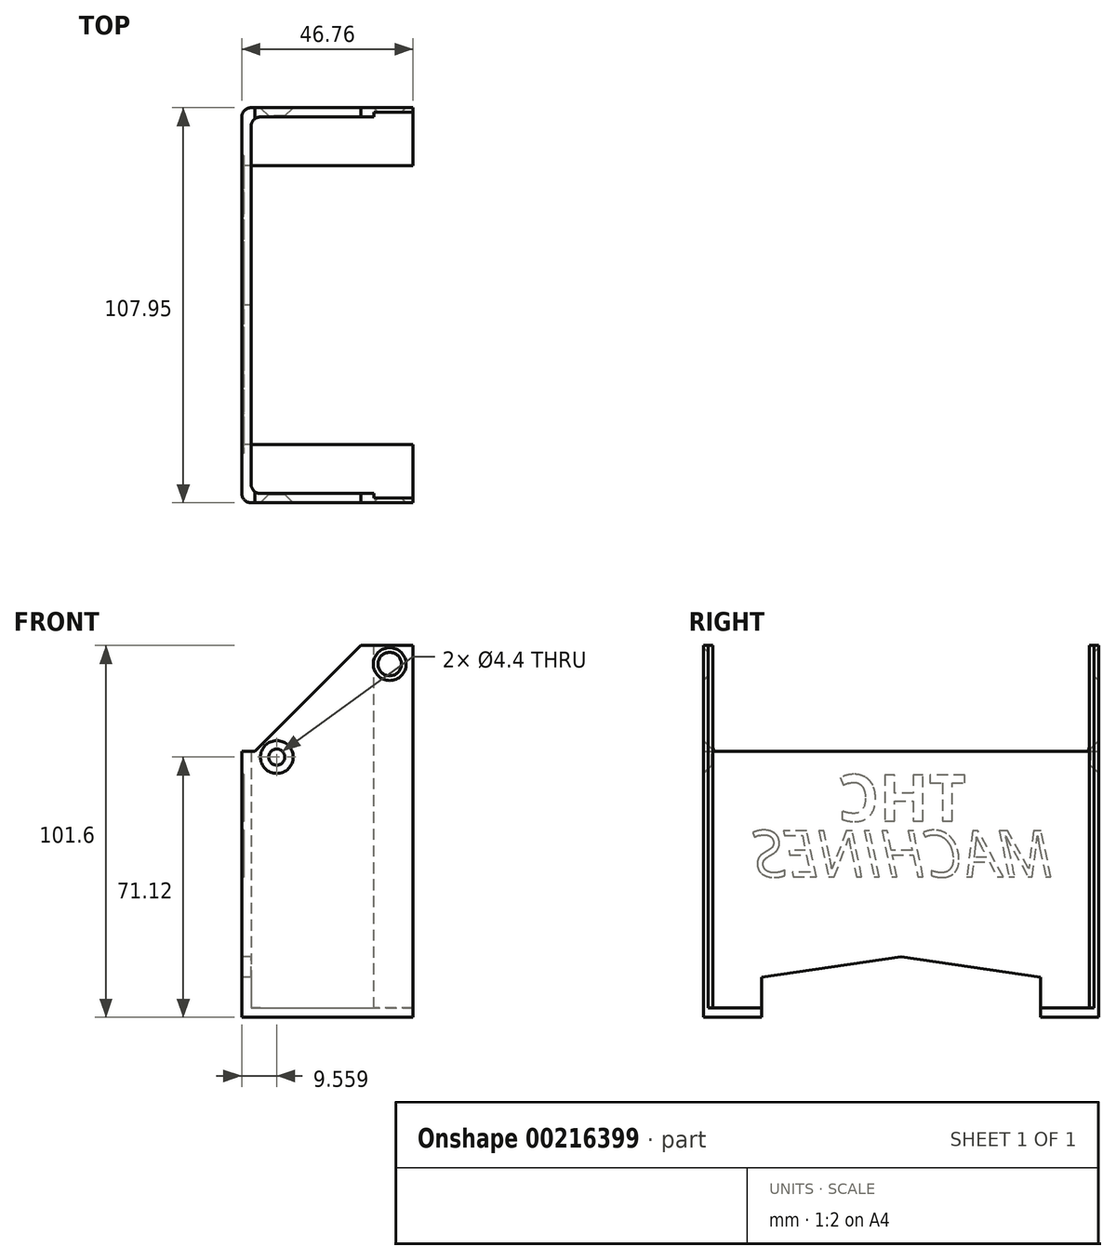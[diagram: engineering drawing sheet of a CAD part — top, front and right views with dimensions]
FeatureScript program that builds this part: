
annotation { "Feature Type Name" : "Feature", "Feature Type Description" : "" }
export const myFeature = defineFeature(function(context is Context, id is Id, definition is map)
    precondition{}
    {
        {
            var Q0;
            Q0=qCreatedBy(makeId("Front.planeOp"),FACE);
            var sketch = newSketch(context, id + "F0", { "sketchPlane" : qUnion([Q0])});
            skLineSegment(sketch, "E0", {"start": v(0, 101.6) * mm, "end": v(-14.28, 101.6) * mm});
            skLineSegment(sketch, "E1", {"start": v(-43.17, 72.7) * mm, "end": v(-46.76, 72.7) * mm});
            skLineSegment(sketch, "E2", {"start": v(-46.76, 72.7) * mm, "end": v(-46.76, 0) * mm});
            skLineSegment(sketch, "E3", {"start": v(-46.76, 0) * mm, "end": v(0, 0) * mm});
            skLineSegment(sketch, "E4", {"start": v(0, 0) * mm, "end": v(0, 101.6) * mm});
            skLineSegment(sketch, "E5", {"start": v(-43.17, 72.7) * mm, "end": v(-14.28, 101.6) * mm});
            skSolve(sketch);
        }
        {
            var Q0;
            Q0 = qSketchRegion(id + "F0", true);
            extrude(context, id + "F1", {"entities" : qUnion([Q0]), "depth" : 107.95 * mm});
        }
        {
            var Q0;
            Q0=makeQuery(id+"F1.opExtrude","SWEPT_FACE",FACE,{"disambiguationData":[OSD([sQuery(id+"F0.wireOp",EDGE,"E0")])]});
            var Q1;
            Q1=makeQuery(id+"F1.opExtrude","SWEPT_FACE",FACE,{"disambiguationData":[OSD([sQuery(id+"F0.wireOp",EDGE,"OUwhYggU-WGUp-ET7a-ehpI-bQHxMFOqMHDO")])]});
            var Q2;
            Q2=makeQuery(id+"F1.opExtrude","SWEPT_FACE",FACE,{"disambiguationData":[OSD([sQuery(id+"F0.wireOp",EDGE,"E4")])]});
            var Q3;
            Q3=makeQuery(id+"F1.opExtrude","SWEPT_FACE",FACE,{"disambiguationData":[OSD([sQuery(id+"F0.wireOp",EDGE,"E5")])]});
            shell(context, id + "F2", {"entities" : qUnion([Q0, Q1, Q2, Q3]), "thickness" : 2.54 * mm});
        }
        {
            var Q0;
            Q0=makeQuery(id+"F1.opExtrude","SWEPT_FACE",FACE,{"disambiguationData":[OSD([sQuery(id+"F0.wireOp",EDGE,"E0")])]});
            var sketch = newSketch(context, id + "F3", { "sketchPlane" : qUnion([Q0])});
            skLineSegment(sketch, "E6.bottom", {"start": v(-10.67, -106.68) * mm, "end": v(22.06, -106.68) * mm});
            skLineSegment(sketch, "E6.top", {"start": v(-10.67, -1.27) * mm, "end": v(22.06, -1.27) * mm});
            skLineSegment(sketch, "E6.left", {"start": v(-10.67, -106.68) * mm, "end": v(-10.67, -1.27) * mm});
            skLineSegment(sketch, "E6.right", {"start": v(22.06, -106.68) * mm, "end": v(22.06, -1.27) * mm});
            skSolve(sketch);
        }
        {
            var Q0;
            Q0=makeQuery(id+"F1.opExtrude","CAP_EDGE",EDGE,{"disambiguationData":[OSD([sQuery(id+"F0.wireOp",EDGE,"E2")])],"isStart":false});
            var Q1;
            Q1=makeQuery(id+"F1.opExtrude","CAP_EDGE",EDGE,{"disambiguationData":[OSD([sQuery(id+"F0.wireOp",EDGE,"E2")])],"isStart":true});
            fillet(context, id + "F4", {"entities" : qUnion([Q0, Q1]), "radius" : 2.54 * mm, "allowEdgeOverflow" : false});
        }
        {
            var Q0;
            Q0 = qSketchRegion(id + "F3", true);
            var Q1;
            Q1=makeQuery(id+"F2.opShell","OFFSET_FACE",FACE,{"disambiguationData":[OSD([sQuery(id+"F0.wireOp",EDGE,"E3")])]});
            extrude(context, id + "F5", {"entities" : qUnion([Q0]), "operationType" : NewBodyOperationType.REMOVE, "endBound" : BoundingType.UP_TO_SURFACE, "oppositeDirection" : true, "endBoundEntityFace" : qUnion([Q1]), "depth" : 25.4 * mm});
        }
        {
            var Q0;
            Q0=makeQuery(id+"F1.opExtrude","CAP_FACE",FACE,{"disambiguationData":[OSD([sQuery(id+"F0.wireOp",EDGE,"E0"),sQuery(id+"F0.wireOp",EDGE,"OUwhYggU-WGUp-ET7a-ehpI-bQHxMFOqMHDO"),sQuery(id+"F0.wireOp",EDGE,"E1"),sQuery(id+"F0.wireOp",EDGE,"E2"),sQuery(id+"F0.wireOp",EDGE,"E3"),sQuery(id+"F0.wireOp",EDGE,"E4")])],"isStart":false});
            var sketch = newSketch(context, id + "F6", { "sketchPlane" : qUnion([Q0])});
            skPoint(sketch, "E7", {"position": v(-6.35, 96.52) * mm});
            skPoint(sketch, "E8", {"position": v(-37.2, 71.12) * mm});
            skSolve(sketch);
        }
        {
            var Q0;
            Q0=sQuery(id+"F6.wireOp",VERTEX,"E8");
            var Q1;
            Q1=sQuery(id+"F6.wireOp",VERTEX,"E7");
            var Q2;
            Q2=makeQuery(id+"F1.opExtrude","SWEPT_BODY",BODY,{"disambiguationData":[OSD([sQuery(id+"F0.wireOp",EDGE,"E0"),sQuery(id+"F0.wireOp",EDGE,"OUwhYggU-WGUp-ET7a-ehpI-bQHxMFOqMHDO"),sQuery(id+"F0.wireOp",EDGE,"E1"),sQuery(id+"F0.wireOp",EDGE,"E2"),sQuery(id+"F0.wireOp",EDGE,"E3"),sQuery(id+"F0.wireOp",EDGE,"E4")])]});
            hole(context, id + "F7", {"style" : HoleStyle.C_SINK, "endStyle" : HoleEndStyle.BLIND, "standardTappedOrClearance" : lookupTablePath({ "standard" : "ISO", "fit" : "Normal", "size" : "M4", "type" : "Clearance" }), "standardBlindInLast" : lookupTablePath({ "fit" : "Standard", "standard" : "ISO", "size" : "M4", "type" : "Clearance" }), "holeDiameter" : 4.4 * mm, "cSinkDiameter" : 8.96 * mm, "cSinkAngle" : 90 * degree, "holeDepth" : 37.19 * mm, "tappedDepth" : 34.92 * mm, "tapClearance" : 3, "locations" : qUnion([Q0, Q1]), "scope" : qUnion([Q2])});
        }
        {
            var Q0;
            Q0=makeQuery(id+"F1.opExtrude","CAP_FACE",FACE,{"disambiguationData":[OSD([sQuery(id+"F0.wireOp",EDGE,"E0"),sQuery(id+"F0.wireOp",EDGE,"OUwhYggU-WGUp-ET7a-ehpI-bQHxMFOqMHDO"),sQuery(id+"F0.wireOp",EDGE,"E1"),sQuery(id+"F0.wireOp",EDGE,"E2"),sQuery(id+"F0.wireOp",EDGE,"E3"),sQuery(id+"F0.wireOp",EDGE,"E4")])],"isStart":true});
            var sketch = newSketch(context, id + "F8", { "sketchPlane" : qUnion([Q0])});
            skPoint(sketch, "E9", {"position": v(6.35, 96.52) * mm});
            skPoint(sketch, "E10", {"position": v(37.2, 71.12) * mm});
            skSolve(sketch);
        }
        {
            var Q0;
            Q0=sQuery(id+"F8.wireOp",VERTEX,"E10");
            var Q1;
            Q1=sQuery(id+"F8.wireOp",VERTEX,"E9");
            var Q2;
            Q2=makeQuery(id+"F1.opExtrude","SWEPT_BODY",BODY,{"disambiguationData":[OSD([sQuery(id+"F0.wireOp",EDGE,"E0"),sQuery(id+"F0.wireOp",EDGE,"OUwhYggU-WGUp-ET7a-ehpI-bQHxMFOqMHDO"),sQuery(id+"F0.wireOp",EDGE,"E1"),sQuery(id+"F0.wireOp",EDGE,"E2"),sQuery(id+"F0.wireOp",EDGE,"E3"),sQuery(id+"F0.wireOp",EDGE,"E4")])]});
            hole(context, id + "F9", {"style" : HoleStyle.C_SINK, "endStyle" : HoleEndStyle.BLIND, "standardTappedOrClearance" : lookupTablePath({ "standard" : "ISO", "fit" : "Normal", "size" : "M4", "type" : "Clearance" }), "standardBlindInLast" : lookupTablePath({ "fit" : "Standard", "standard" : "ISO", "size" : "M4", "type" : "Clearance" }), "holeDiameter" : 4.4 * mm, "cSinkDiameter" : 8.96 * mm, "cSinkAngle" : 90 * degree, "holeDepth" : 37.19 * mm, "tappedDepth" : 34.92 * mm, "tapClearance" : 3, "locations" : qUnion([Q0, Q1]), "scope" : qUnion([Q2])});
        }
        {
            var Q0;
            Q0=makeQuery(id+"F1.opExtrude","SWEPT_FACE",FACE,{"disambiguationData":[OSD([sQuery(id+"F0.wireOp",EDGE,"E2")])]});
            var sketch = newSketch(context, id + "F10", { "sketchPlane" : qUnion([Q0])});
            skLineSegment(sketch, "E11.bottom", {"start": v(15.88, 0) * mm, "end": v(92.08, 0) * mm});
            skLineSegment(sketch, "E11.top", {"start": v(15.88, 10.92) * mm, "end": v(92.08, 10.92) * mm});
            skLineSegment(sketch, "E11.left", {"start": v(15.88, 0) * mm, "end": v(15.88, 10.92) * mm});
            skLineSegment(sketch, "E11.right", {"start": v(92.08, 0) * mm, "end": v(92.08, 10.92) * mm});
            skLineSegment(sketch, "E12", {"start": v(0, 0) * mm, "end": v(15.88, 0) * mm});
            skLineSegment(sketch, "E13", {"start": v(92.08, 0) * mm, "end": v(107.95, 0) * mm});
            skLineSegment(sketch, "E14", {"start": v(15.87, 10.92) * mm, "end": v(53.98, 16.51) * mm});
            skPoint(sketch, "E14.endSnap0", {"position": v(53.98, 10.92) * mm});
            skLineSegment(sketch, "E15", {"start": v(53.97, 16.51) * mm, "end": v(92.08, 10.92) * mm});
            skSolve(sketch);
        }
        {
            var Q0;
            Q0=makeQuery(id+"F10.imprint","IMPRINT",FACE,{"disambiguationData":[TD([[makeQuery(id+"F10.imprint","IMPRINT",EDGE,{"derivedFrom":sQuery(id+"F10.wireOp",EDGE,"E11.top")}),1.0]])]});
            var Q1;
            Q1=makeQuery(id+"F10.imprint","IMPRINT",FACE,{"disambiguationData":[TD([[makeQuery(id+"F10.imprint","IMPRINT",EDGE,{"derivedFrom":sQuery(id+"F10.wireOp",EDGE,"E11.bottom")}),-1.0]])]});
            extrude(context, id + "F11", {"entities" : qUnion([Q0, Q1]), "operationType" : NewBodyOperationType.REMOVE, "oppositeDirection" : true, "depth" : 56.13 * mm});
        }
        {
            var Q0;
            Q0=makeQuery(id+"F1.opExtrude","SWEPT_FACE",FACE,{"disambiguationData":[OSD([sQuery(id+"F0.wireOp",EDGE,"E2")])]});
            var sketch = newSketch(context, id + "F12", { "sketchPlane" : qUnion([Q0])});
            skText(sketch, "E16", { "text": "THC", "fontName": "OpenSans-Bold.ttf"});
            skLineSegment(sketch, "E17", {"start": v(53.98, 72.7) * mm, "end": v(53.98, 66.36) * mm});
            skText(sketch, "E18", { "text": "MACHINES", "fontName": "OpenSans-Italic.ttf"});
            skLineSegment(sketch, "E19", {"start": v(53.97, 53.66) * mm, "end": v(53.97, 51.12) * mm});
            const initialGuessF12  = {"E16": [0.03624, 0.05366, 1, 0, 0.0127], "E18": [0.01232, 0.03842, 1, 0, 0.0127]};
            skSetInitialGuess(sketch, initialGuessF12);
            skSolve(sketch);
        }
        {
            var Q0;
            Q0 = qSketchRegion(id + "F12", true);
            extrude(context, id + "F13", {"entities" : qUnion([Q0]), "operationType" : NewBodyOperationType.REMOVE, "oppositeDirection" : true, "depth" : 0.53 * mm});
        }
        {
            var Q0;
            Q0=makeQuery(id+"F1.opExtrude","SWEPT_FACE",FACE,{"disambiguationData":[OSD([sQuery(id+"F0.wireOp",EDGE,"E1")])]});
            var sketch = newSketch(context, id + "F14", { "sketchPlane" : qUnion([Q0])});
            skLineSegment(sketch, "E20.bottom", {"start": v(-44.22, -2.54) * mm, "end": v(-29.04, -2.54) * mm});
            skLineSegment(sketch, "E20.top", {"start": v(-44.22, -105.4) * mm, "end": v(-29.04, -105.4) * mm});
            skLineSegment(sketch, "E20.left", {"start": v(-44.22, -2.54) * mm, "end": v(-44.22, -105.4) * mm});
            skLineSegment(sketch, "E20.right", {"start": v(-29.04, -2.54) * mm, "end": v(-29.04, -105.4) * mm});
            skPoint(sketch, "E21.visualSharp", {"position": v(-44.22, -2.54) * mm});
            skSolve(sketch);
        }
        {
            var Q0;
            Q0 = qSketchRegion(id + "F14", true);
            var Q1;
            {var subQ0=sQuery(id+"F3.wireOp",EDGE,"E6.top");var subQ1=makeQuery(id+"F5.opExtrude","SWEPT_FACE",FACE,{"disambiguationData":[OSD([subQ0])]});var subQ5=sQuery(id+"F0.wireOp",EDGE,"E3");var subQ9=makeQuery(id+"F2.opShell","OFFSET_FACE",FACE,{"disambiguationData":[OSD([subQ5])]});var subQ10=sQuery(id+"F3.wireOp",EDGE,"E6.left");var subQ11=makeQuery(id+"F5.opExtrude","CAP_FACE",FACE,{"disambiguationData":[OSD([sQuery(id+"F3.wireOp",EDGE,"E6.bottom"),subQ0,subQ10,sQuery(id+"F3.wireOp",EDGE,"E6.right")])],"isStart":false});Q1=makeQuery(id+"F11.boolean.opBoolean","SPLIT",FACE,{"disambiguationData":[TD([makeQuery(id+"F5.boolean.opBoolean","COPY",FACE,{"derivedFrom":subQ1})])],"derivedFrom":makeQuery(id+"F5.boolean.opBoolean","MERGE",FACE,{"derivedFrom":[subQ9],"fromTools":[subQ11]})});}
            extrude(context, id + "F15", {"entities" : qUnion([Q0]), "operationType" : NewBodyOperationType.REMOVE, "endBound" : BoundingType.UP_TO_SURFACE, "oppositeDirection" : true, "endBoundEntityFace" : qUnion([Q1]), "depth" : 25.4 * mm});
        }
        {
            var Q0;
            Q0 = qSketchRegion(id + "F14", true);
            var Q1;
            {var subQ0=sQuery(id+"F3.wireOp",EDGE,"E6.bottom");var subQ1=makeQuery(id+"F5.opExtrude","SWEPT_FACE",FACE,{"disambiguationData":[OSD([subQ0])]});var subQ5=sQuery(id+"F0.wireOp",EDGE,"E3");var subQ9=makeQuery(id+"F2.opShell","OFFSET_FACE",FACE,{"disambiguationData":[OSD([subQ5])]});var subQ10=sQuery(id+"F3.wireOp",EDGE,"E6.left");var subQ11=makeQuery(id+"F5.opExtrude","CAP_FACE",FACE,{"disambiguationData":[OSD([subQ0,sQuery(id+"F3.wireOp",EDGE,"E6.top"),subQ10,sQuery(id+"F3.wireOp",EDGE,"E6.right")])],"isStart":false});Q1=makeQuery(id+"F11.boolean.opBoolean","SPLIT",FACE,{"disambiguationData":[TD([makeQuery(id+"F5.boolean.opBoolean","COPY",FACE,{"derivedFrom":subQ1})])],"derivedFrom":makeQuery(id+"F5.boolean.opBoolean","MERGE",FACE,{"derivedFrom":[subQ9],"fromTools":[subQ11]})});}
            extrude(context, id + "F16", {"entities" : qUnion([Q0]), "operationType" : NewBodyOperationType.REMOVE, "endBound" : BoundingType.UP_TO_SURFACE, "oppositeDirection" : true, "endBoundEntityFace" : qUnion([Q1]), "depth" : 25.4 * mm});
        }
        {
            var Q0;
            {var subQ0=sQuery(id+"F0.wireOp",EDGE,"E2");Q0=makeQuery(id+"F15.boolean.opBoolean","MERGE",EDGE,{"derivedFrom":[makeQuery(id+"F2.opShell","OFFSET_EDGE",EDGE,{"disambiguationData":[OSD([subQ0]),TDD([makeQuery(id+"F1.opExtrude","CAP_EDGE",EDGE,{"disambiguationData":[OSD([subQ0])],"isStart":true})])]}),makeQuery(id+"F15.opExtrude","SWEPT_EDGE",EDGE,{"disambiguationData":[OSD([sQuery(id+"F14.wireOp",EDGE,"E20.bottom"),sQuery(id+"F14.wireOp",EDGE,"E20.left")])]})]});}
            var Q1;
            {var subQ0=sQuery(id+"F0.wireOp",EDGE,"E2");Q1=makeQuery(id+"F15.boolean.opBoolean","MERGE",EDGE,{"derivedFrom":[makeQuery(id+"F2.opShell","OFFSET_EDGE",EDGE,{"disambiguationData":[OSD([subQ0]),TDD([makeQuery(id+"F1.opExtrude","CAP_EDGE",EDGE,{"disambiguationData":[OSD([subQ0])],"isStart":false})])]}),makeQuery(id+"F15.opExtrude","SWEPT_EDGE",EDGE,{"disambiguationData":[OSD([sQuery(id+"F14.wireOp",EDGE,"E20.top"),sQuery(id+"F14.wireOp",EDGE,"E20.left")])]})]});}
            fillet(context, id + "F17", {"entities" : qUnion([Q0, Q1]), "radius" : 2.54 * mm, "allowEdgeOverflow" : false});
        }
    });
